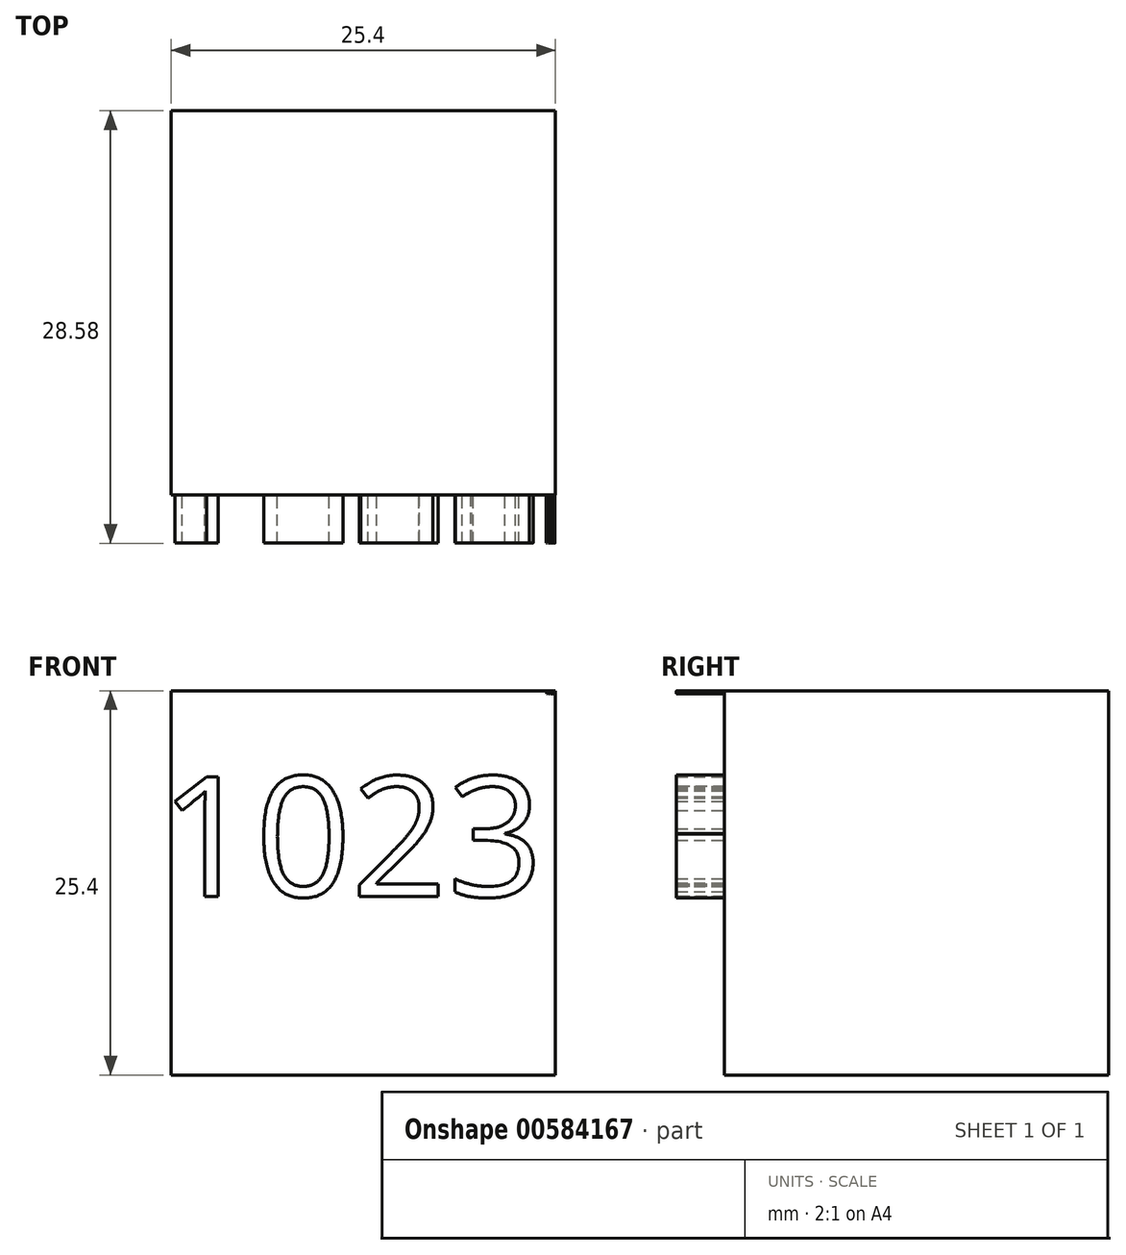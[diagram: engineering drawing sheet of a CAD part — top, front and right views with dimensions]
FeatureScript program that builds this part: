
annotation { "Feature Type Name" : "Feature", "Feature Type Description" : "" }
export const myFeature = defineFeature(function(context is Context, id is Id, definition is map)
    precondition{}
    {
        {
            var Q0;
            Q0=qCreatedBy(makeId("Front.planeOp"),FACE);
            var sketch = newSketch(context, id + "F0", { "sketchPlane" : qUnion([Q0])});
            skLineSegment(sketch, "E0.bottom", {"start": v(-12.7, 12.7) * mm, "end": v(12.7, 12.7) * mm});
            skLineSegment(sketch, "E0.top", {"start": v(-12.7, -12.7) * mm, "end": v(12.7, -12.7) * mm});
            skLineSegment(sketch, "E0.left", {"start": v(-12.7, 12.7) * mm, "end": v(-12.7, -12.7) * mm});
            skLineSegment(sketch, "E0.right", {"start": v(12.7, 12.7) * mm, "end": v(12.7, -12.7) * mm});
            skPoint(sketch, "E0.middle", {"position": v(0, 0) * mm});
            skSolve(sketch);
        }
        {
            var Q0;
            Q0 = qSketchRegion(id + "F0", true);
            extrude(context, id + "F1", {"entities" : qUnion([Q0]), "depth" : 25.4 * mm, "offsetDistance" : 25.4 * mm});
        }
        {
            var Q0;
            Q0=makeQuery(id+"F1.opExtrude","CAP_FACE",FACE,{"disambiguationData":[OSD([sQuery(id+"F0.wireOp",EDGE,"E0.bottom"),sQuery(id+"F0.wireOp",EDGE,"E0.top"),sQuery(id+"F0.wireOp",EDGE,"E0.left"),sQuery(id+"F0.wireOp",EDGE,"E0.right")])],"isStart":false});
            var sketch = newSketch(context, id + "F2", { "sketchPlane" : qUnion([Q0])});
            skText(sketch, "E1", { "text": "1023", "fontName": "OpenSans-Regular.ttf"});
            skText(sketch, "E2", { "text": "1023", "fontName": "OpenSans-Regular.ttf"});
            const initialGuessF2  = {"E1": [0.01205, 0.0125, 1, 0, 0.0002], "E2": [-0.01347, -0.0009, 1, 0, 0.00798]};
            skSetInitialGuess(sketch, initialGuessF2);
            skSolve(sketch);
        }
        {
            var Q0;
            Q0 = qSketchRegion(id + "F2", true);
            extrude(context, id + "F3", {"entities" : qUnion([Q0]), "operationType" : NewBodyOperationType.ADD, "depth" : 3.17 * mm, "offsetDistance" : 25.4 * mm});
        }
    });
